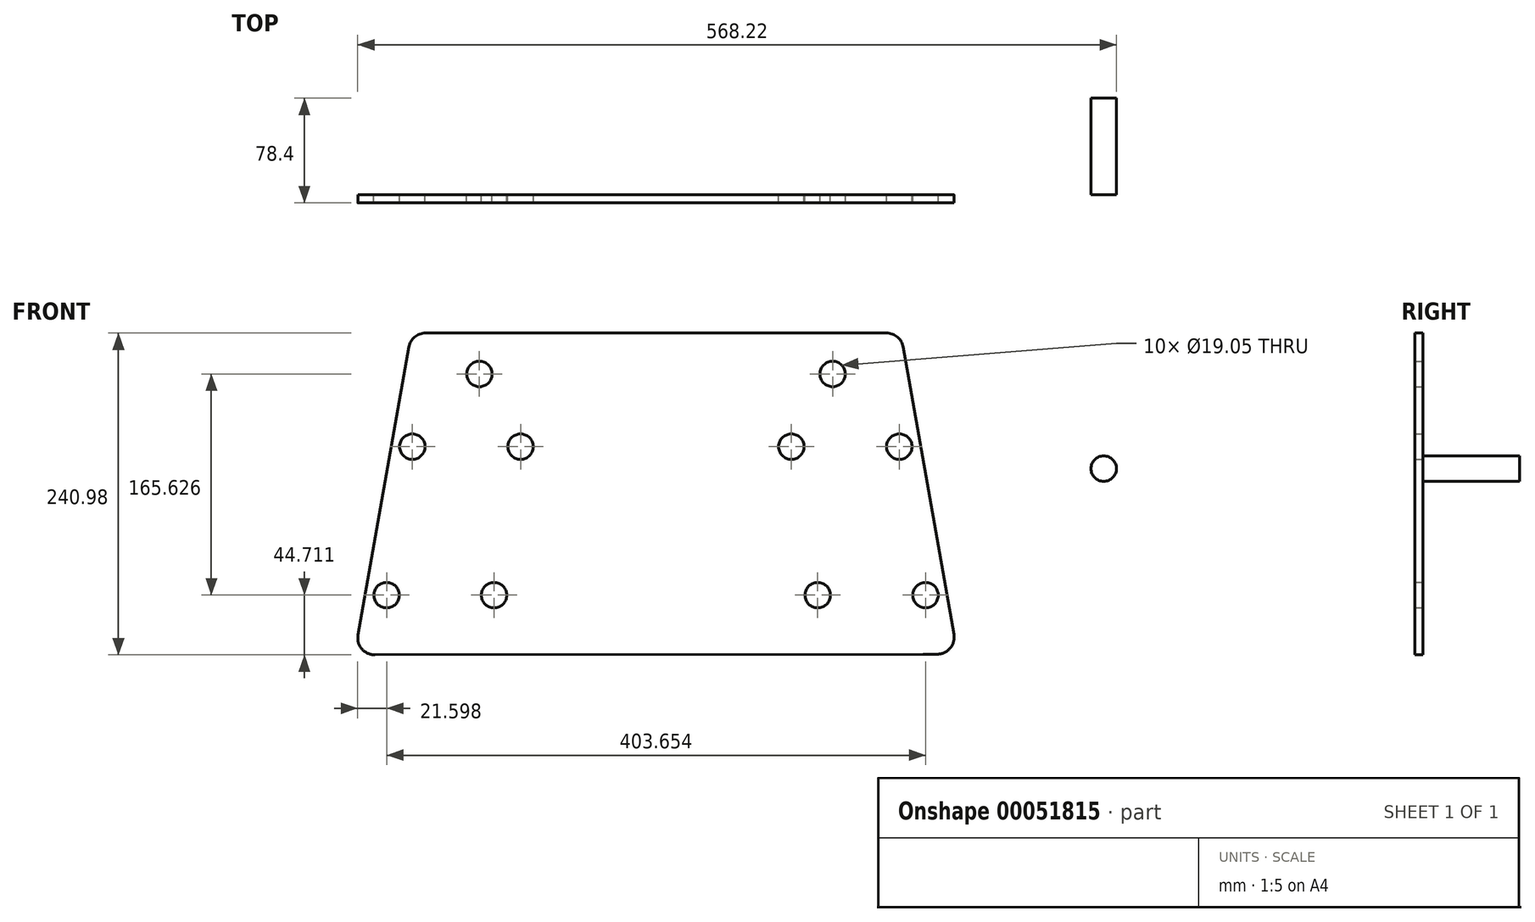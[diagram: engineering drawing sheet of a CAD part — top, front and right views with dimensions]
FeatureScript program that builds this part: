
annotation { "Feature Type Name" : "Feature", "Feature Type Description" : "" }
export const myFeature = defineFeature(function(context is Context, id is Id, definition is map)
    precondition{}
    {
        {
            var Q0;
            Q0=qCreatedBy(makeId("Front.planeOp"),FACE);
            var sketch = newSketch(context, id + "F0", { "sketchPlane" : qUnion([Q0])});
            skLineSegment(sketch, "E0", {"start": v(0, 110.7) * mm, "end": v(0, -110.28) * mm, "construction": true});
            skLineSegment(sketch, "E1.0", {"start": v(-101.6, 110.7) * mm, "end": v(-101.6, -110.28) * mm, "construction": true});
            skLineSegment(sketch, "E2.0", {"start": v(101.6, 110.7) * mm, "end": v(101.6, -110.28) * mm, "construction": true});
            skLineSegment(sketch, "E3", {"start": v(-101.6, 110.7) * mm, "end": v(-141.32, -114.56) * mm, "construction": true});
            skLineSegment(sketch, "E4", {"start": v(101.6, 110.7) * mm, "end": v(141.22, -114.02) * mm, "construction": true});
            skLineSegment(sketch, "E5.0", {"start": v(161.08, 121.18) * mm, "end": v(200.7, -103.53) * mm, "construction": true});
            skLineSegment(sketch, "E6.0", {"start": v(-161.08, 121.18) * mm, "end": v(-200.8, -104.07) * mm, "construction": true});
            skLineSegment(sketch, "E7", {"start": v(101.6, 110.7) * mm, "end": v(162.93, 110.7) * mm, "construction": true});
            skLineSegment(sketch, "E8", {"start": v(-251.82, 56.3) * mm, "end": v(249.57, 56.3) * mm, "construction": true});
            skLineSegment(sketch, "E9", {"start": v(-254.77, -54.93) * mm, "end": v(267.26, -54.93) * mm, "construction": true});
            skLineSegment(sketch, "E10.0", {"start": v(172.66, 141.34) * mm, "end": v(-172.66, 141.34) * mm});
            skLineSegment(sketch, "E11.0", {"start": v(185.17, 130.85) * mm, "end": v(223.1, -84.24) * mm});
            skLineSegment(sketch, "E12.0", {"start": v(-185.17, 130.85) * mm, "end": v(-223.18, -84.74) * mm});
            skLineSegment(sketch, "E13", {"start": v(-210.66, -99.64) * mm, "end": v(199.94, -99.16) * mm});
            skPoint(sketch, "E14.orphan", {"position": v(231.13, -99.12) * mm});
            skLineSegment(sketch, "E15", {"start": v(199.94, -99.16) * mm, "end": v(210.6, -99.15) * mm});
            skLineSegment(sketch, "E16.trimOffspring", {"start": v(-101.6, 110.7) * mm, "end": v(-162.93, 110.7) * mm, "construction": true});
            skPoint(sketch, "E17.orphan", {"position": v(-95.5, 110.7) * mm});
            skCircle(sketch, "E18", {"center": v(-132.27, 110.7) * mm, "radius": 9.53 * mm});
            skCircle(sketch, "E19", {"center": v(132.27, 110.7) * mm, "radius": 9.53 * mm});
            skCircle(sketch, "E20", {"center": v(182.2, 56.3) * mm, "radius": 9.53 * mm});
            skCircle(sketch, "E21", {"center": v(101.39, 56.3) * mm, "radius": 9.53 * mm});
            skCircle(sketch, "E22", {"center": v(201.87, -54.93) * mm, "radius": 9.53 * mm});
            skCircle(sketch, "E23", {"center": v(121.08, -54.93) * mm, "radius": 9.53 * mm});
            skCircle(sketch, "E24", {"center": v(-182.49, 56.3) * mm, "radius": 9.53 * mm});
            skCircle(sketch, "E25", {"center": v(-101.46, 56.3) * mm, "radius": 9.53 * mm});
            skCircle(sketch, "E26", {"center": v(-121.32, -54.93) * mm, "radius": 9.53 * mm});
            skCircle(sketch, "E27", {"center": v(-201.78, -54.93) * mm, "radius": 9.53 * mm});
            skPoint(sketch, "E28.visualSharp", {"position": v(-183.32, 141.34) * mm});
            skArc(sketch, "E28.filletArc", {"start": v(-172.66, 141.34) * mm, "mid": v(-180.83, 138.37) * mm, "end": v(-185.17, 130.85) * mm});
            skPoint(sketch, "E29.visualSharp", {"position": v(-225.81, -99.66) * mm});
            skArc(sketch, "E29.filletArc", {"start": v(-223.18, -84.74) * mm, "mid": v(-220.4, -95.11) * mm, "end": v(-210.66, -99.64) * mm});
            skPoint(sketch, "E30.visualSharp", {"position": v(225.72, -99.12) * mm});
            skArc(sketch, "E30.filletArc", {"start": v(210.6, -99.15) * mm, "mid": v(220.32, -94.6) * mm, "end": v(223.1, -84.24) * mm});
            skPoint(sketch, "E31.visualSharp", {"position": v(183.32, 141.34) * mm});
            skArc(sketch, "E31.filletArc", {"start": v(185.17, 130.85) * mm, "mid": v(180.83, 138.37) * mm, "end": v(172.66, 141.34) * mm});
            skSolve(sketch);
        }
        {
            var Q0;
            Q0 = qSketchRegion(id + "F0", true);
            extrude(context, id + "F1", {"entities" : qUnion([Q0]), "depth" : 6 * mm});
        }
        {
            var Q0;
            Q0=makeQuery(id+"F1.opExtrude","CAP_FACE",FACE,{"disambiguationData":[OSD([sQuery(id+"F0.wireOp",EDGE,"E10.0"),sQuery(id+"F0.wireOp",EDGE,"E11.0"),sQuery(id+"F0.wireOp",EDGE,"E12.0"),sQuery(id+"F0.wireOp",EDGE,"E13"),sQuery(id+"F0.wireOp",EDGE,"E15"),sQuery(id+"F0.wireOp",EDGE,"E18"),sQuery(id+"F0.wireOp",EDGE,"E19"),sQuery(id+"F0.wireOp",EDGE,"E20"),sQuery(id+"F0.wireOp",EDGE,"E21"),sQuery(id+"F0.wireOp",EDGE,"E22"),sQuery(id+"F0.wireOp",EDGE,"E23"),sQuery(id+"F0.wireOp",EDGE,"E24"),sQuery(id+"F0.wireOp",EDGE,"E25"),sQuery(id+"F0.wireOp",EDGE,"E26"),sQuery(id+"F0.wireOp",EDGE,"E27"),sQuery(id+"F0.wireOp",EDGE,"E28.filletArc"),sQuery(id+"F0.wireOp",EDGE,"E29.filletArc"),sQuery(id+"F0.wireOp",EDGE,"E30.filletArc"),sQuery(id+"F0.wireOp",EDGE,"E31.filletArc")])],"isStart":true});
            var sketch = newSketch(context, id + "F2", { "sketchPlane" : qUnion([Q0])});
            skCircle(sketch, "E32", {"center": v(-335.31, 39.85) * mm, "radius": 9.53 * mm});
            skSolve(sketch);
        }
        {
            var Q0;
            Q0 = qSketchRegion(id + "F2", true);
            extrude(context, id + "F3", {"entities" : qUnion([Q0]), "depth" : 72.4 * mm});
        }
    });
